# Revit family: Cameo 2.7
name_source: partatom
category: Lighting Fixtures
revit_build: Autodesk Revit 2017 (Build: 20170419_0315(x64)
units: mm (PartAtom-declared; Revit-internal decimal feet)

## family parameters
Cut with Voids When Loaded = Yes
Host = Face
Light Source = No
Part Type = Normal
Room Calculation Point = Yes
Round Connector Dimension = Use Diameter
Shared = No

## types (6) — shared parameters
Apparent Load Phase 1 = 5 W
Body = L&L_White anodized aluminium
CRI = 90
Code = CM2700100050SN Black; CM2700100050SE White
Control system = -
Cutout dimensions = diam. 65 mm
Default Elevation = 1219.2 mm  [stored 4 ft]
Delivered lumen output = 303 lm (3000K, 32°)
Description = Recessed for indoor applications
Energy efficiency class = A A+ A++
Features = -
Frame = L&L_Black anodized
Geometry 1 = Cameo2.7_fixed
Geometry 2 = Cameo2.7_mod : Cameo 2.7
Geometry 3 = Cameo2.7_frame
Height mm = 48 mm
Height void = 50 mm  [stored 0.164042 ft]
Horizontal rotation max = 360.00°
IP = 40
L1 = 10.5 mm  [stored 0.0344488 ft]
LED Colour = 3000K (also available: 2700K and 4000K - ref. URL Technical sheet)
Length mm = 69 mm  [stored 0.226378 ft]
Lens = L&L_Tempered extra-clear glass
Lumen output at source = 452 lm (3000K)
Manufacturer = L&L Luce&Light
Material = body and trim in aluminium
Model = Cameo 2.7
Mounting = recessed (ceilings, and false ceilings and niches in plasterboard)
No. and type of led = 1 power LED High Intensity, 3-step MacAdam, 50 000h L95 B10 (Ta 25°C)
Notes = The light beam can be precisely directed thanks to the great adjustability of the optical unit: rotation up to 360° around the vertical axis and 20° along the horizontal axis
Power = 5W
Power cables = includes 1.5 m PVC cable FROR 2x0.35/0.35 Ø3.5 m
Power supply = 24Vdc
Power supply unit = not included
Radius void = 28.65 mm
Springs = L&L_C 67 annealed steel
URL = https://www.lucelight.it
URL Accessories and power supply units = https://www.lucelight.it
URL Catalogue = -
URL DXF = https://www.lucelight.it
URL Description = https://www.lucelight.it
URL General code = https://www.lucelight.it
URL IES Photometric file = https://www.lucelight.it
URL Image = https://www.lucelight.it
URL Technical sheet = https://www.lucelight.it
Vertical Rotation max = 20.00°
Vertical rotation max = 20.00°
Vertical rotation min = -20.00°
Voltage = 24 V
Weight kg = 0.15 kg
Width mm = 69 mm  [stored 0.226378 ft]
Wiring = parallel

## per-type parameters (varying)
| type | Light Source | Optics |
| Cameo 2.7_J 65° (3000K 5W 24Vdc) | Light Source : J65° | 65° |
| Cameo 2.7_L 32° (3000K 5W 24Vdc) | Light Source : L32° | 32° |
| Cameo 2.7_M 17° (3000K 5W 24Vdc) | Light Source : M17° | 17° |
| Cameo 2.7_P 19° (3000K 5W 24Vdc) | Light Source : P19° | 19° |
| Cameo 2.7_S 11° (3000K 5W 24Vdc) | Light Source : S11° | 11° |
| Cameo 2.7_W 13°x43° (3000K 5W 24Vdc) | Light Source : W13°x43° | 13°x43° |

note: [stored X ft] marks values corroborated as IEEE doubles in the binary element streams (Revit-internal decimal feet)

## geometry (parser evidence)
native form markers: Blend x2, Sweep x15
no freeform markers — native parametric forms only
